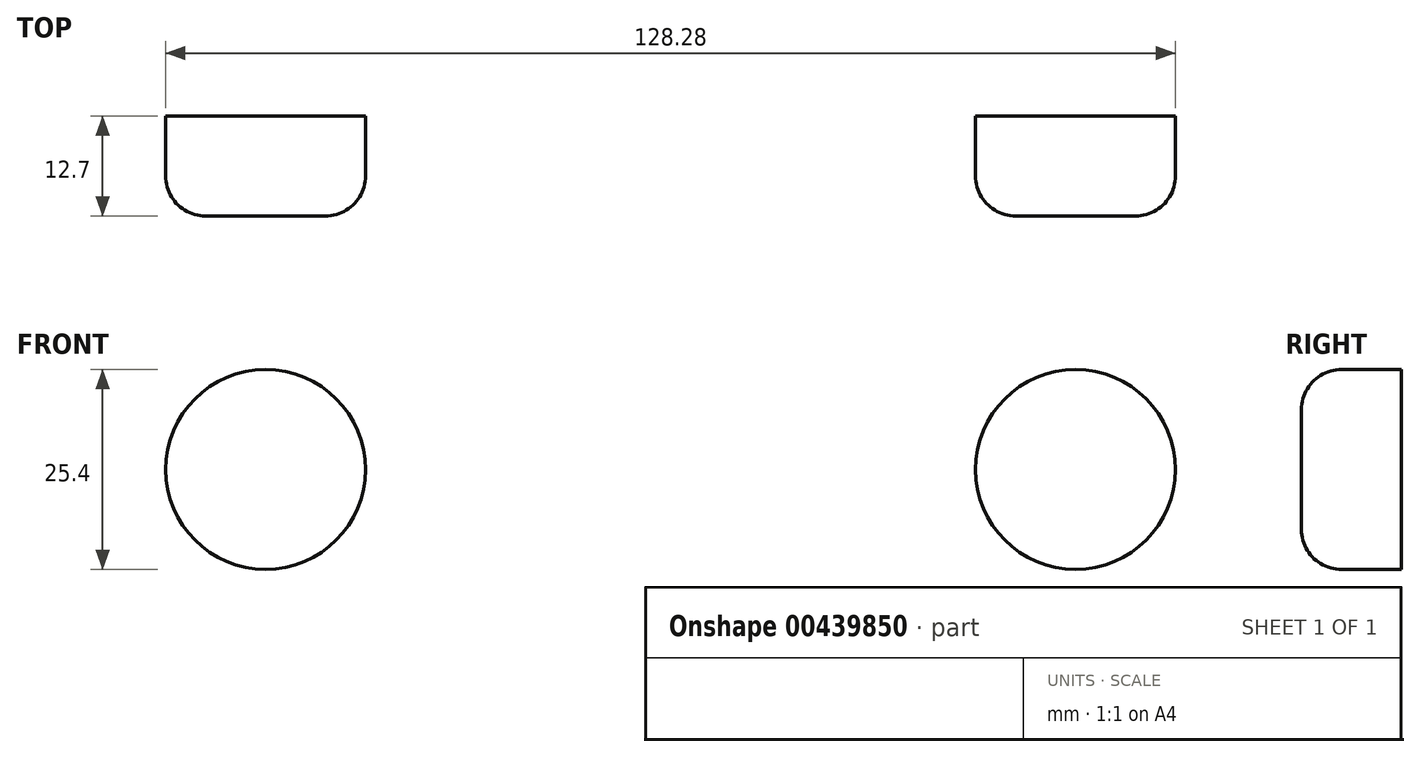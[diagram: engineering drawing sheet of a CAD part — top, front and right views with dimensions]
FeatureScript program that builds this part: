
annotation { "Feature Type Name" : "Feature", "Feature Type Description" : "" }
export const myFeature = defineFeature(function(context is Context, id is Id, definition is map)
    precondition{}
    {
        {
            var Q0;
            Q0=qCreatedBy(makeId("Front.planeOp"),FACE);
            var sketch = newSketch(context, id + "F0", { "sketchPlane" : qUnion([Q0])});
            skCircle(sketch, "E0", {"center": v(-51.44, 0) * mm, "radius": 12.7 * mm});
            skCircle(sketch, "E1", {"center": v(51.44, 0) * mm, "radius": 12.7 * mm});
            skSolve(sketch);
        }
        {
            var Q0;
            Q0 = qSketchRegion(id + "F0", true);
            extrude(context, id + "F1", {"entities" : qUnion([Q0]), "depth" : 12.7 * mm});
        }
        {
            var Q0;
            Q0=makeQuery(id+"F1.opExtrude","CAP_FACE",FACE,{"disambiguationData":[OSD([sQuery(id+"F0.wireOp",EDGE,"E0")])],"isStart":false});
            var Q1;
            Q1=makeQuery(id+"F1.opExtrude","CAP_FACE",FACE,{"disambiguationData":[OSD([sQuery(id+"F0.wireOp",EDGE,"E1")])],"isStart":false});
            fillet(context, id + "F2", {"entities" : qUnion([Q0, Q1]), "radius" : 5.08 * mm, "tangentPropagation" : true, "allowEdgeOverflow" : false});
        }
    });
